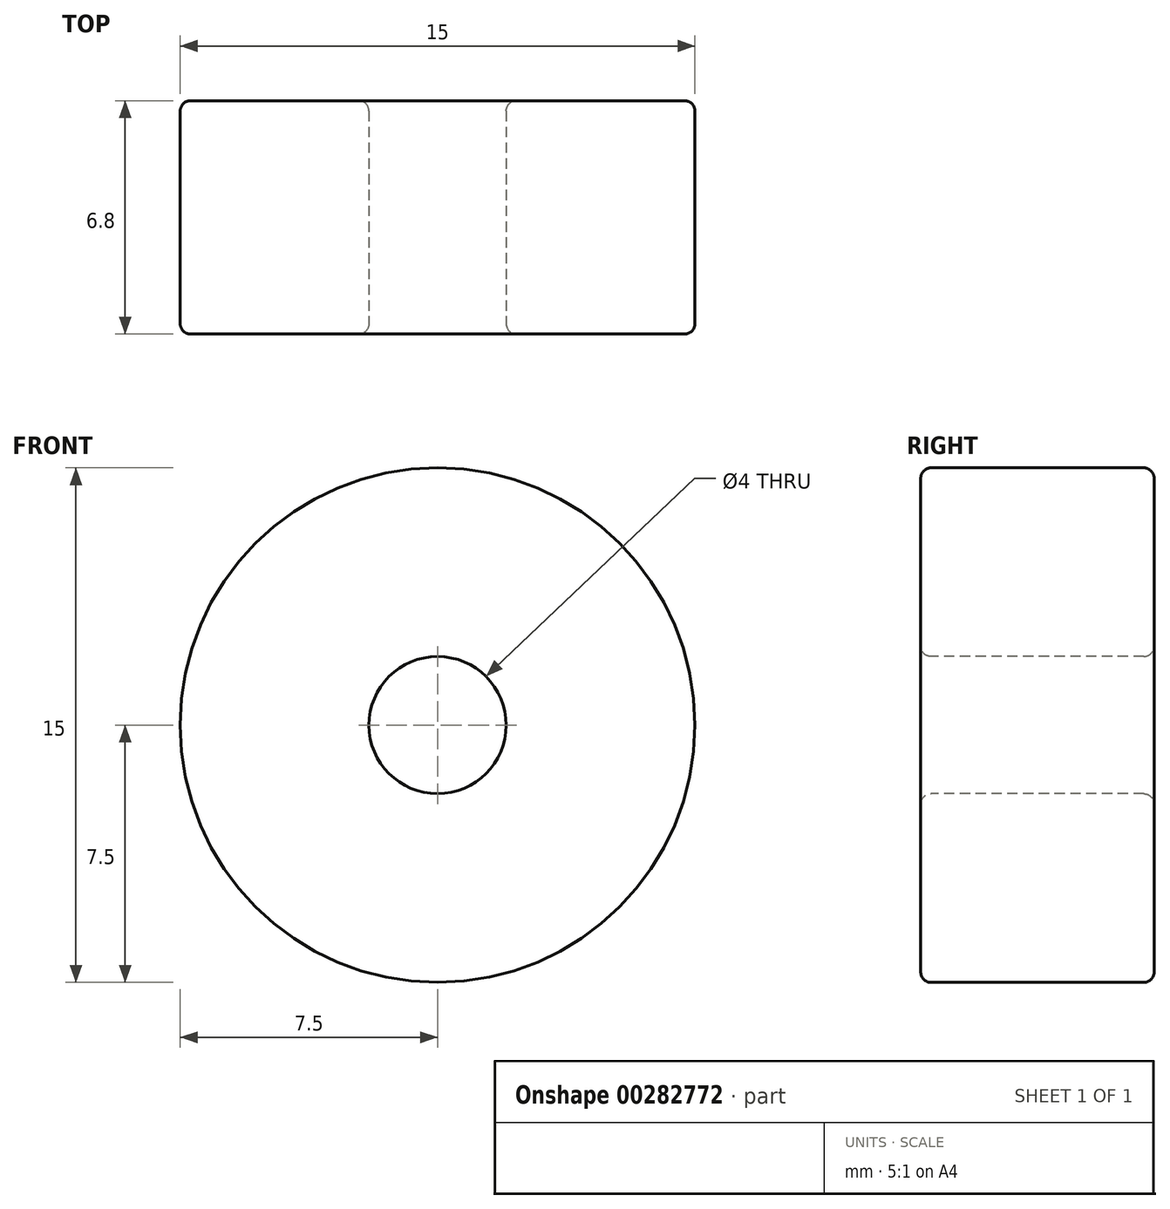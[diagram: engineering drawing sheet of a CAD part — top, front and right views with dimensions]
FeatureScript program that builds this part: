
annotation { "Feature Type Name" : "Feature", "Feature Type Description" : "" }
export const myFeature = defineFeature(function(context is Context, id is Id, definition is map)
    precondition{}
    {
        {
            var Q0;
            Q0=qCreatedBy(makeId("Front.planeOp"),FACE);
            var sketch = newSketch(context, id + "F0", { "sketchPlane" : qUnion([Q0])});
            skCircle(sketch, "E0", {"center": v(0, 0) * mm, "radius": 7.5 * mm});
            skSolve(sketch);
        }
        {
            var Q0;
            Q0 = qSketchRegion(id + "F0", true);
            extrude(context, id + "F1", {"entities" : qUnion([Q0]), "oppositeDirection" : true, "depth" : 6.8 * mm});
        }
        {
            var Q0;
            Q0=makeQuery(id+"F1.opExtrude","CAP_FACE",FACE,{"disambiguationData":[OSD([sQuery(id+"F0.wireOp",EDGE,"E0")])],"isStart":true});
            var sketch = newSketch(context, id + "F2", { "sketchPlane" : qUnion([Q0])});
            skCircle(sketch, "E1", {"center": v(0, 0) * mm, "radius": 2 * mm});
            skSolve(sketch);
        }
        {
            var Q0;
            Q0 = qSketchRegion(id + "F2", true);
            extrude(context, id + "F3", {"entities" : qUnion([Q0]), "operationType" : NewBodyOperationType.REMOVE, "oppositeDirection" : true, "depth" : 24.4 * mm});
        }
        {
            var Q0;
            Q0=makeQuery(id+"F1.opExtrude","CAP_FACE",FACE,{"disambiguationData":[OSD([sQuery(id+"F0.wireOp",EDGE,"E0")])],"isStart":true});
            var Q1;
            Q1=makeQuery(id+"F1.opExtrude","CAP_EDGE",EDGE,{"disambiguationData":[OSD([sQuery(id+"F0.wireOp",EDGE,"E0")])],"isStart":false});
            fillet(context, id + "F4", {"entities" : qUnion([Q0, Q1]), "radius" : 0.3 * mm, "tangentPropagation" : true, "allowEdgeOverflow" : false});
        }
        {
            var Q0;
            Q0=makeQuery(id+"F3.boolean.opBoolean","INTERSECT",EDGE,{"derivedFrom":[makeQuery(id+"F1.opExtrude","CAP_FACE",FACE,{"disambiguationData":[OSD([sQuery(id+"F0.wireOp",EDGE,"E0")])],"isStart":false}),makeQuery(id+"F3.opExtrude","SWEPT_FACE",FACE,{"disambiguationData":[OSD([sQuery(id+"F2.wireOp",EDGE,"E1")])]})]});
            fillet(context, id + "F5", {"entities" : qUnion([Q0]), "radius" : 0.3 * mm, "tangentPropagation" : true, "allowEdgeOverflow" : false});
        }
    });
